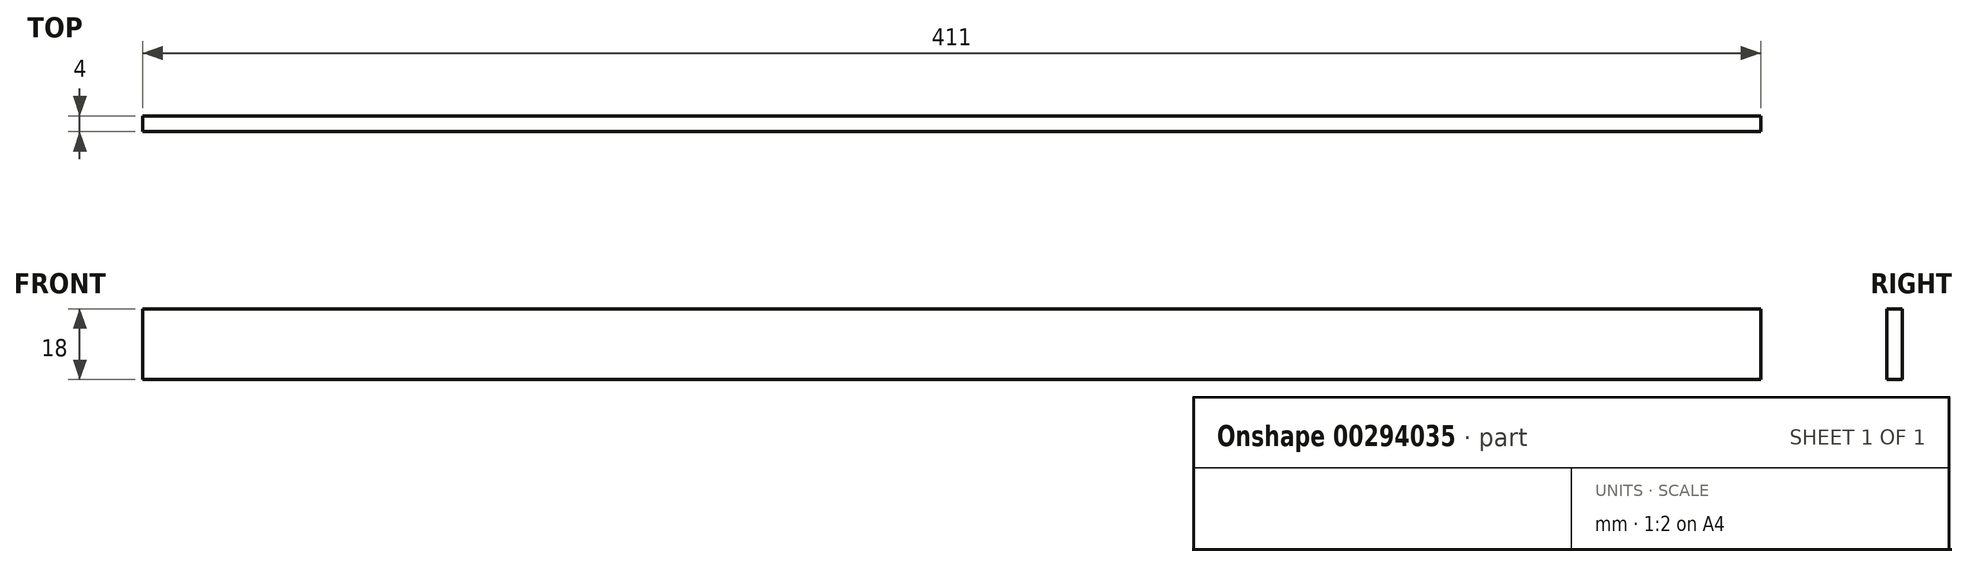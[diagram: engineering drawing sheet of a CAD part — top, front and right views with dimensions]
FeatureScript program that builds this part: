
annotation { "Feature Type Name" : "Feature", "Feature Type Description" : "" }
export const myFeature = defineFeature(function(context is Context, id is Id, definition is map)
    precondition{}
    {
        {
            var Q0;
            Q0=qCreatedBy(makeId("Front.planeOp"),FACE);
            var sketch = newSketch(context, id + "F0", { "sketchPlane" : qUnion([Q0])});
            skLineSegment(sketch, "E0.bottom", {"start": v(205.5, 9) * mm, "end": v(-205.5, 9) * mm});
            skLineSegment(sketch, "E0.top", {"start": v(205.5, -9) * mm, "end": v(-205.5, -9) * mm});
            skLineSegment(sketch, "E0.left", {"start": v(205.5, 9) * mm, "end": v(205.5, -9) * mm});
            skLineSegment(sketch, "E0.right", {"start": v(-205.5, 9) * mm, "end": v(-205.5, -9) * mm});
            skPoint(sketch, "E0.middle", {"position": v(0, 0) * mm});
            skSolve(sketch);
        }
        {
            var Q0;
            Q0=makeQuery(id+"F0.imprint","IMPRINT",FACE,{"disambiguationData":[TD([[makeQuery(id+"F0.imprint","IMPRINT",EDGE,{"derivedFrom":sQuery(id+"F0.wireOp",EDGE,"E0.bottom")}),1.0]])]});
            extrude(context, id + "F1", {"entities" : qUnion([Q0]), "depth" : 4 * mm});
        }
    });
